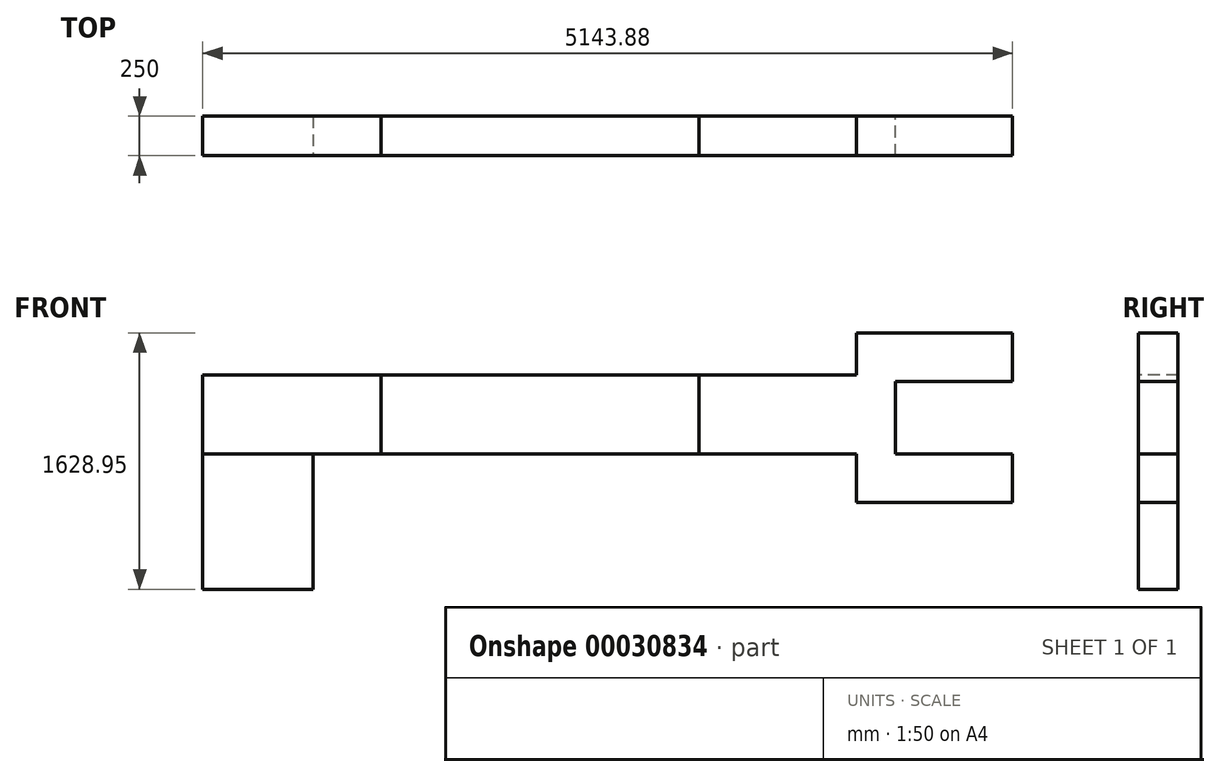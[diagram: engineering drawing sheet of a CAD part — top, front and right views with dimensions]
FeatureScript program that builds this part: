
annotation { "Feature Type Name" : "Feature", "Feature Type Description" : "" }
export const myFeature = defineFeature(function(context is Context, id is Id, definition is map)
    precondition{}
    {
        {
            var Q0;
            Q0=qCreatedBy(makeId("Front.planeOp"),FACE);
            var sketch = newSketch(context, id + "F0", { "sketchPlane" : qUnion([Q0])});
            skCircle(sketch, "E0", {"center": v(0, 1110) * mm, "radius": 80 * mm});
            skLineSegment(sketch, "E1", {"start": v(0, 0) * mm, "end": v(-350, 0) * mm});
            skLineSegment(sketch, "E2", {"start": v(-350, 0) * mm, "end": v(-350, 860) * mm});
            skLineSegment(sketch, "E3", {"start": v(-350, 860) * mm, "end": v(-57.8, 1165.31) * mm});
            skLineSegment(sketch, "E4", {"start": v(0, 1110) * mm, "end": v(0, 0) * mm, "construction": true});
            skLineSegment(sketch, "E5.MirrorCS", {"start": v(350, 860) * mm, "end": v(57.8, 1165.31) * mm});
            skLineSegment(sketch, "E6.MirrorCS", {"start": v(350, 0) * mm, "end": v(350, 860) * mm});
            skLineSegment(sketch, "E7.MirrorCS", {"start": v(0, 0) * mm, "end": v(350, 0) * mm, "construction": true});
            skLineSegment(sketch, "E8.MirrorCS", {"start": v(0, 0) * mm, "end": v(350, 0) * mm});
            skLineSegment(sketch, "E9.MirrorCS", {"start": v(-350, 0) * mm, "end": v(-350, 860) * mm, "construction": true});
            skLineSegment(sketch, "E10.rect.bottom", {"start": v(-350, 860) * mm, "end": v(1033.4, 860) * mm});
            skLineSegment(sketch, "E10.rect.top", {"start": v(-350, 1360) * mm, "end": v(1033.4, 1360) * mm});
            skLineSegment(sketch, "E10.rect.left", {"start": v(-350, 860) * mm, "end": v(-350, 1360) * mm});
            skLineSegment(sketch, "E10.rect.right", {"start": v(1033.4, 860) * mm, "end": v(1033.4, 1360) * mm});
            skPoint(sketch, "E10.rect.middle", {"position": v(341.7, 1110) * mm});
            skCircle(sketch, "E11", {"center": v(1033.4, 1110) * mm, "radius": 250 * mm});
            skLineSegment(sketch, "E12.rect.bottom", {"start": v(3051.03, 860) * mm, "end": v(783.4, 860) * mm});
            skLineSegment(sketch, "E12.rect.top", {"start": v(3051.03, 1360) * mm, "end": v(783.4, 1360) * mm});
            skLineSegment(sketch, "E12.rect.left", {"start": v(3051.03, 860) * mm, "end": v(3051.03, 1360) * mm});
            skLineSegment(sketch, "E12.rect.right", {"start": v(783.4, 860) * mm, "end": v(783.4, 1360) * mm});
            skPoint(sketch, "E12.rect.middle", {"position": v(1917.21, 1110) * mm});
            skCircle(sketch, "E13", {"center": v(3051.03, 1110) * mm, "radius": 250 * mm});
            skLineSegment(sketch, "E14.rect.bottom", {"start": v(3801.03, 860) * mm, "end": v(2801.03, 860) * mm});
            skLineSegment(sketch, "E14.rect.top", {"start": v(3801.03, 1360) * mm, "end": v(2801.03, 1360) * mm});
            skLineSegment(sketch, "E14.rect.left", {"start": v(3801.03, 860) * mm, "end": v(3801.03, 1360) * mm});
            skLineSegment(sketch, "E14.rect.right", {"start": v(2801.03, 860) * mm, "end": v(2801.03, 1360) * mm});
            skPoint(sketch, "E14.rect.middle", {"position": v(3301.03, 1110) * mm});
            skSolve(sketch);
        }
        {
            var Q0;
            Q0=makeQuery(id+"F0.imprint","IMPRINT",FACE,{"disambiguationData":[TD([[makeQuery(id+"F0.imprint","IMPRINT",EDGE,{"derivedFrom":sQuery(id+"F0.wireOp",EDGE,"E1")}),-1.0]])]});
            extrude(context, id + "F1", {"entities" : qUnion([Q0]), "oppositeDirection" : true, "depth" : 250 * mm});
        }
        {
            var Q0;
            {var subQ6=sQuery(id+"F0.wireOp",EDGE,"E3");Q0=makeQuery(id+"F0.imprint","IMPRINT",FACE,{"disambiguationData":[TD([[makeQuery(id+"F0.imprint","IMPRINT",EDGE,{"derivedFrom":subQ6}),1.0]])]});}
            var Q1;
            {var subQ2=sQuery(id+"F0.wireOp",EDGE,"E3");Q1=makeQuery(id+"F0.imprint","IMPRINT",FACE,{"disambiguationData":[TD([[makeQuery(id+"F0.imprint","IMPRINT",EDGE,{"derivedFrom":subQ2}),-1.0]])]});}
            var Q2;
            {var subQ0=sQuery(id+"F0.wireOp",EDGE,"E0");var subQ2=makeQuery(id+"F0.imprint","INTERSECT",VERTEX,{"derivedFrom":[subQ0,sQuery(id+"F0.wireOp",EDGE,"E3")]});Q2=makeQuery(id+"F0.imprint","IMPRINT",FACE,{"disambiguationData":[TD([[makeQuery(id+"F0.imprint","IMPRINT",EDGE,{"disambiguationData":[TD([[subQ2,1.0]])],"derivedFrom":subQ0}),1.0]])]});}
            extrude(context, id + "F2", {"entities" : qUnion([Q0, Q1, Q2]), "oppositeDirection" : true, "depth" : 250 * mm});
        }
        {
            var Q0;
            {var subQ0=sQuery(id+"F0.wireOp",EDGE,"E12.rect.right");var subQ1=sQuery(id+"F0.wireOp",EDGE,"E11");var subQ2=makeQuery(id+"F0.imprint","INTERSECT",VERTEX,{"derivedFrom":[subQ1,subQ0]});Q0=makeQuery(id+"F0.imprint","IMPRINT",FACE,{"disambiguationData":[TD([[makeQuery(id+"F0.imprint","IMPRINT",EDGE,{"disambiguationData":[TD([[subQ2,1.0]])],"derivedFrom":subQ1}),-1.0]])]});}
            var Q1;
            {var subQ1=sQuery(id+"F0.wireOp",EDGE,"E11");var subQ3=sQuery(id+"F0.wireOp",EDGE,"E12.rect.right");var subQ5=makeQuery(id+"F0.imprint","INTERSECT",VERTEX,{"derivedFrom":[subQ1,subQ3]});Q1=makeQuery(id+"F0.imprint","IMPRINT",FACE,{"disambiguationData":[TD([[makeQuery(id+"F0.imprint","IMPRINT",EDGE,{"disambiguationData":[TD([[subQ5,-1.0]])],"derivedFrom":subQ1}),-1.0]])]});}
            var Q2;
            {var subQ2=sQuery(id+"F0.wireOp",EDGE,"E10.rect.right");Q2=makeQuery(id+"F0.imprint","IMPRINT",FACE,{"disambiguationData":[TD([[makeQuery(id+"F0.imprint","IMPRINT",EDGE,{"derivedFrom":subQ2}),1.0]])]});}
            var Q3;
            {var subQ1=sQuery(id+"F0.wireOp",EDGE,"E10.rect.right");Q3=makeQuery(id+"F0.imprint","IMPRINT",FACE,{"disambiguationData":[TD([[makeQuery(id+"F0.imprint","IMPRINT",EDGE,{"derivedFrom":subQ1}),-1.0]])]});}
            var Q4;
            {var subQ0=sQuery(id+"F0.wireOp",EDGE,"E14.rect.right");var subQ1=makeQuery(id+"F0.imprint","INTERSECT",VERTEX,{"derivedFrom":[sQuery(id+"F0.wireOp",EDGE,"E13"),subQ0]});Q4=makeQuery(id+"F0.imprint","IMPRINT",FACE,{"disambiguationData":[TD([[makeQuery(id+"F0.imprint","IMPRINT",EDGE,{"disambiguationData":[TD([[subQ1,1.0]])],"derivedFrom":subQ0}),1.0]])]});}
            extrude(context, id + "F3", {"entities" : qUnion([Q0, Q1, Q2, Q3, Q4]), "oppositeDirection" : true, "depth" : 250 * mm});
        }
        {
            var Q0;
            {var subQ0=sQuery(id+"F0.wireOp",EDGE,"E14.rect.right");var subQ1=sQuery(id+"F0.wireOp",EDGE,"E13");var subQ2=makeQuery(id+"F0.imprint","INTERSECT",VERTEX,{"derivedFrom":[subQ1,subQ0]});Q0=makeQuery(id+"F0.imprint","IMPRINT",FACE,{"disambiguationData":[TD([[makeQuery(id+"F0.imprint","IMPRINT",EDGE,{"disambiguationData":[TD([[subQ2,-1.0]])],"derivedFrom":subQ1}),-1.0]])]});}
            var Q1;
            {var subQ1=sQuery(id+"F0.wireOp",EDGE,"E12.rect.left");Q1=makeQuery(id+"F0.imprint","IMPRINT",FACE,{"disambiguationData":[TD([[makeQuery(id+"F0.imprint","IMPRINT",EDGE,{"derivedFrom":subQ1}),-1.0]])]});}
            var Q2;
            {var subQ2=sQuery(id+"F0.wireOp",EDGE,"E12.rect.left");Q2=makeQuery(id+"F0.imprint","IMPRINT",FACE,{"disambiguationData":[TD([[makeQuery(id+"F0.imprint","IMPRINT",EDGE,{"derivedFrom":subQ2}),1.0]])]});}
            var Q3;
            {var subQ1=sQuery(id+"F0.wireOp",EDGE,"E13");var subQ3=sQuery(id+"F0.wireOp",EDGE,"E14.rect.right");var subQ5=makeQuery(id+"F0.imprint","INTERSECT",VERTEX,{"derivedFrom":[subQ1,subQ3]});Q3=makeQuery(id+"F0.imprint","IMPRINT",FACE,{"disambiguationData":[TD([[makeQuery(id+"F0.imprint","IMPRINT",EDGE,{"disambiguationData":[TD([[subQ5,1.0]])],"derivedFrom":subQ1}),-1.0]])]});}
            var Q4;
            {var subQ0=sQuery(id+"F0.wireOp",EDGE,"E14.rect.left");Q4=makeQuery(id+"F0.imprint","IMPRINT",FACE,{"disambiguationData":[TD([[makeQuery(id+"F0.imprint","IMPRINT",EDGE,{"derivedFrom":subQ0}),1.0]])]});}
            extrude(context, id + "F4", {"entities" : qUnion([Q0, Q1, Q2, Q3, Q4]), "oppositeDirection" : true, "depth" : 250 * mm});
        }
        {
            var Q0;
            Q0=makeQuery(id+"F4.opExtrude","SWEPT_FACE",FACE,{"disambiguationData":[OSD([sQuery(id+"F0.wireOp",EDGE,"E14.rect.left")])]});
            var sketch = newSketch(context, id + "F5", { "sketchPlane" : qUnion([Q0])});
            skLineSegment(sketch, "E15.bottom", {"start": v(0, 1628.95) * mm, "end": v(250, 1628.95) * mm});
            skLineSegment(sketch, "E15.top", {"start": v(0, 549.83) * mm, "end": v(250, 549.83) * mm});
            skLineSegment(sketch, "E15.left", {"start": v(0, 1628.95) * mm, "end": v(0, 549.83) * mm});
            skLineSegment(sketch, "E15.right", {"start": v(250, 1628.95) * mm, "end": v(250, 549.83) * mm});
            skSolve(sketch);
        }
        {
            var Q0;
            Q0 = qSketchRegion(id + "F5", true);
            extrude(context, id + "F6", {"entities" : qUnion([Q0]), "operationType" : NewBodyOperationType.ADD, "depth" : 250 * mm});
        }
        {
            var Q0;
            {var subQ0=sQuery(id+"F0.wireOp",EDGE,"E14.rect.left");Q0=makeQuery(id+"F0.imprint","IMPRINT",FACE,{"disambiguationData":[TD([[makeQuery(id+"F0.imprint","IMPRINT",EDGE,{"derivedFrom":subQ0}),1.0]])]});}
            var sketch = newSketch(context, id + "F7", { "sketchPlane" : qUnion([Q0])});
            skLineSegment(sketch, "E16.bottom", {"start": v(3801.03, 1628.95) * mm, "end": v(4793.88, 1628.95) * mm});
            skLineSegment(sketch, "E16.top", {"start": v(3801.03, 1318.78) * mm, "end": v(4793.88, 1318.78) * mm});
            skLineSegment(sketch, "E16.left", {"start": v(3801.03, 1628.95) * mm, "end": v(3801.03, 1318.78) * mm});
            skLineSegment(sketch, "E16.right", {"start": v(4793.88, 1628.95) * mm, "end": v(4793.88, 1318.78) * mm});
            skLineSegment(sketch, "E17.bottom", {"start": v(3801.03, 860) * mm, "end": v(4793.88, 860) * mm});
            skLineSegment(sketch, "E17.top", {"start": v(3801.03, 549.83) * mm, "end": v(4793.88, 549.83) * mm});
            skLineSegment(sketch, "E17.left", {"start": v(3801.03, 860) * mm, "end": v(3801.03, 549.83) * mm});
            skLineSegment(sketch, "E17.right", {"start": v(4793.88, 860) * mm, "end": v(4793.88, 549.83) * mm});
            skSolve(sketch);
        }
        {
            var Q0;
            Q0 = qSketchRegion(id + "F7", true);
            extrude(context, id + "F8", {"entities" : qUnion([Q0]), "operationType" : NewBodyOperationType.ADD, "oppositeDirection" : true, "depth" : 250 * mm});
        }
    });
